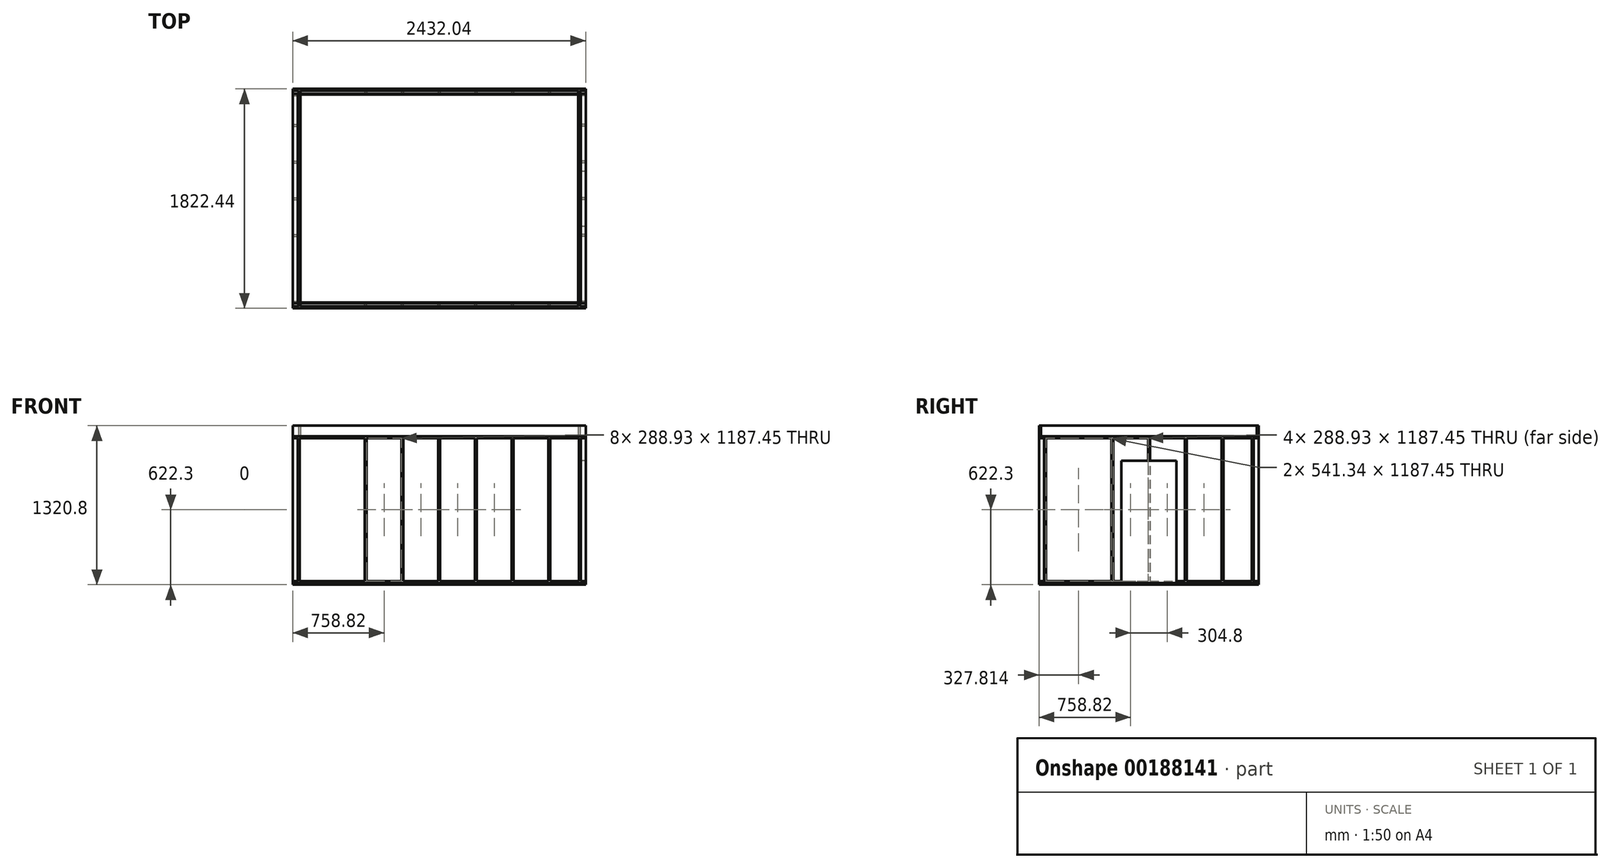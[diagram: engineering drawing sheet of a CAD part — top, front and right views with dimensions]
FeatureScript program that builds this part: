
annotation { "Feature Type Name" : "Feature", "Feature Type Description" : "" }
export const myFeature = defineFeature(function(context is Context, id is Id, definition is map)
    precondition{}
    {
        {
            var Q0;
            Q0=qCreatedBy(makeId("Top.planeOp"),FACE);
            var sketch = newSketch(context, id + "F0", { "sketchPlane" : qUnion([Q0])});
            skLineSegment(sketch, "E0.bottom", {"start": v(1174.75, 869.95) * mm, "end": v(-1174.75, 869.95) * mm});
            skLineSegment(sketch, "E0.top", {"start": v(1174.75, -869.95) * mm, "end": v(-1174.75, -869.95) * mm});
            skLineSegment(sketch, "E0.left", {"start": v(1174.75, 869.95) * mm, "end": v(1174.75, -869.95) * mm});
            skLineSegment(sketch, "E0.right", {"start": v(-1174.75, 869.95) * mm, "end": v(-1174.75, -869.95) * mm});
            skPoint(sketch, "E0.middle", {"position": v(0, 0) * mm});
            skLineSegment(sketch, "E1.0", {"start": v(1168.4, 863.6) * mm, "end": v(-1168.4, 863.6) * mm});
            skLineSegment(sketch, "E1.1", {"start": v(1168.4, 863.6) * mm, "end": v(1168.4, -863.6) * mm});
            skLineSegment(sketch, "E1.2", {"start": v(1168.4, -863.6) * mm, "end": v(-1168.4, -863.6) * mm});
            skLineSegment(sketch, "E1.3", {"start": v(-1168.4, 863.6) * mm, "end": v(-1168.4, -863.6) * mm});
            skSolve(sketch);
        }
        {
            var Q0;
            Q0 = qSketchRegion(id + "F0", true);
            extrude(context, id + "F1", {"entities" : qUnion([Q0]), "depth" : 1219.2 * mm});
        }
        {
            var Q0;
            Q0=makeQuery(id+"F1.opExtrude","SWEPT_FACE",FACE,{"disambiguationData":[OSD([sQuery(id+"F0.wireOp",EDGE,"E0.top")])]});
            var sketch = newSketch(context, id + "F2", { "sketchPlane" : qUnion([Q0])});
            skLineSegment(sketch, "E2.bottom", {"start": v(-1216.03, 0) * mm, "end": v(1216.03, 0) * mm});
            skLineSegment(sketch, "E2.top", {"start": v(-1216.03, 15.87) * mm, "end": v(1216.03, 15.87) * mm});
            skLineSegment(sketch, "E2.left", {"start": v(-1216.03, 0) * mm, "end": v(-1216.03, 15.87) * mm});
            skLineSegment(sketch, "E2.right", {"start": v(1216.03, 0) * mm, "end": v(1216.03, 15.87) * mm});
            skLineSegment(sketch, "E3.bottom", {"start": v(1216.03, 1219.2) * mm, "end": v(-1216.03, 1219.2) * mm});
            skLineSegment(sketch, "E3.top", {"start": v(1216.03, 1203.33) * mm, "end": v(-1216.03, 1203.32) * mm});
            skLineSegment(sketch, "E3.left", {"start": v(1216.03, 1219.2) * mm, "end": v(1216.03, 1203.33) * mm});
            skLineSegment(sketch, "E3.right", {"start": v(-1216.03, 1219.2) * mm, "end": v(-1216.03, 1203.32) * mm});
            skLineSegment(sketch, "E4.bottom", {"start": v(-1174.75, 1203.32) * mm, "end": v(-1158.88, 1203.32) * mm});
            skLineSegment(sketch, "E4.top", {"start": v(-1174.75, 15.87) * mm, "end": v(-1158.88, 15.87) * mm});
            skLineSegment(sketch, "E4.left", {"start": v(-1174.75, 1203.32) * mm, "end": v(-1174.75, 15.87) * mm});
            skLineSegment(sketch, "E4.right", {"start": v(-1158.88, 1203.32) * mm, "end": v(-1158.88, 15.87) * mm});
            skLineSegment(sketch, "E5.bottom", {"start": v(1174.75, 1203.33) * mm, "end": v(1158.88, 1203.33) * mm});
            skLineSegment(sketch, "E5.top", {"start": v(1174.75, 15.87) * mm, "end": v(1158.88, 15.87) * mm});
            skLineSegment(sketch, "E5.left", {"start": v(1174.75, 1203.33) * mm, "end": v(1174.75, 15.87) * mm});
            skLineSegment(sketch, "E5.right", {"start": v(1158.88, 1203.33) * mm, "end": v(1158.88, 15.88) * mm});
            skLineSegment(sketch, "E6.bottom", {"start": v(-922.34, 1203.32) * mm, "end": v(-906.46, 1203.32) * mm});
            skLineSegment(sketch, "E6.top", {"start": v(-922.34, 15.87) * mm, "end": v(-906.46, 15.87) * mm});
            skLineSegment(sketch, "E6.left", {"start": v(-922.34, 1203.33) * mm, "end": v(-922.34, 15.87) * mm});
            skLineSegment(sketch, "E6.right", {"start": v(-906.46, 1203.33) * mm, "end": v(-906.46, 15.87) * mm});
            skLineSegment(sketch, "E7.1.0.0", {"start": v(-601.66, 1203.33) * mm, "end": v(-601.66, 15.87) * mm});
            skLineSegment(sketch, "E7.1.0.1", {"start": v(-617.54, 1203.33) * mm, "end": v(-617.54, 15.87) * mm});
            skLineSegment(sketch, "E7.1.0.2", {"start": v(-617.54, 1203.32) * mm, "end": v(-601.66, 1203.32) * mm});
            skLineSegment(sketch, "E7.1.0.3", {"start": v(-617.54, 15.87) * mm, "end": v(-601.66, 15.87) * mm});
            skLineSegment(sketch, "E7.2.0.0", {"start": v(-296.86, 1203.33) * mm, "end": v(-296.86, 15.87) * mm});
            skLineSegment(sketch, "E7.2.0.1", {"start": v(-312.74, 1203.33) * mm, "end": v(-312.74, 15.87) * mm});
            skLineSegment(sketch, "E7.2.0.2", {"start": v(-312.74, 1203.32) * mm, "end": v(-296.86, 1203.32) * mm});
            skLineSegment(sketch, "E7.2.0.3", {"start": v(-312.74, 15.87) * mm, "end": v(-296.86, 15.87) * mm});
            skLineSegment(sketch, "E7.3.0.0", {"start": v(7.94, 1203.33) * mm, "end": v(7.94, 15.87) * mm});
            skLineSegment(sketch, "E7.3.0.1", {"start": v(-7.94, 1203.33) * mm, "end": v(-7.94, 15.87) * mm});
            skLineSegment(sketch, "E7.3.0.2", {"start": v(-7.94, 1203.32) * mm, "end": v(7.94, 1203.32) * mm});
            skLineSegment(sketch, "E7.3.0.3", {"start": v(-7.94, 15.87) * mm, "end": v(7.94, 15.87) * mm});
            skLineSegment(sketch, "E7.4.0.0", {"start": v(312.74, 1203.33) * mm, "end": v(312.74, 15.87) * mm});
            skLineSegment(sketch, "E7.4.0.1", {"start": v(296.86, 1203.33) * mm, "end": v(296.86, 15.87) * mm});
            skLineSegment(sketch, "E7.4.0.2", {"start": v(296.86, 1203.32) * mm, "end": v(312.74, 1203.32) * mm});
            skLineSegment(sketch, "E7.4.0.3", {"start": v(296.86, 15.87) * mm, "end": v(312.74, 15.87) * mm});
            skLineSegment(sketch, "E7.5.0.0", {"start": v(617.54, 1203.33) * mm, "end": v(617.54, 15.87) * mm});
            skLineSegment(sketch, "E7.5.0.1", {"start": v(601.66, 1203.33) * mm, "end": v(601.66, 15.87) * mm});
            skLineSegment(sketch, "E7.5.0.2", {"start": v(601.66, 1203.32) * mm, "end": v(617.54, 1203.32) * mm});
            skLineSegment(sketch, "E7.5.0.3", {"start": v(601.66, 15.87) * mm, "end": v(617.54, 15.87) * mm});
            skLineSegment(sketch, "E7.6.0.0", {"start": v(922.34, 1203.33) * mm, "end": v(922.34, 15.87) * mm});
            skLineSegment(sketch, "E7.6.0.1", {"start": v(906.46, 1203.33) * mm, "end": v(906.46, 15.87) * mm});
            skLineSegment(sketch, "E7.6.0.2", {"start": v(906.46, 1203.32) * mm, "end": v(922.34, 1203.32) * mm});
            skLineSegment(sketch, "E7.6.0.3", {"start": v(906.46, 15.87) * mm, "end": v(922.34, 15.87) * mm});
            skLineSegment(sketch, "E7.direction1", {"start": v(-906.46, 15.87) * mm, "end": v(-601.66, 15.87) * mm, "construction": true});
            skLineSegment(sketch, "E8", {"start": v(-1158.88, 609.6) * mm, "end": v(-922.34, 609.6) * mm, "construction": true});
            skLineSegment(sketch, "E9", {"start": v(922.34, 609.6) * mm, "end": v(1158.88, 609.6) * mm, "construction": true});
            skSolve(sketch);
        }
        {
            var Q0;
            Q0 = qSketchRegion(id + "F2", true);
            var Q1;
            Q1=makeQuery(id+"F2.imprint","IMPRINT",FACE,{"disambiguationData":[TD([[makeQuery(id+"F2.imprint","IMPRINT",EDGE,{"derivedFrom":sQuery(id+"F2.wireOp",EDGE,"E6.bottom")}),-1.0]])]});
            var Q2;
            Q2=makeQuery(id+"F2.imprint","IMPRINT",FACE,{"disambiguationData":[TD([[makeQuery(id+"F2.imprint","IMPRINT",EDGE,{"derivedFrom":sQuery(id+"F2.wireOp",EDGE,"E7.1.0.0")}),-1.0]])]});
            var Q3;
            Q3=makeQuery(id+"F2.imprint","IMPRINT",FACE,{"disambiguationData":[TD([[makeQuery(id+"F2.imprint","IMPRINT",EDGE,{"derivedFrom":sQuery(id+"F2.wireOp",EDGE,"E7.2.0.0")}),-1.0]])]});
            var Q4;
            Q4=makeQuery(id+"F2.imprint","IMPRINT",FACE,{"disambiguationData":[TD([[makeQuery(id+"F2.imprint","IMPRINT",EDGE,{"derivedFrom":sQuery(id+"F2.wireOp",EDGE,"E7.3.0.0")}),-1.0]])]});
            var Q5;
            Q5=makeQuery(id+"F2.imprint","IMPRINT",FACE,{"disambiguationData":[TD([[makeQuery(id+"F2.imprint","IMPRINT",EDGE,{"derivedFrom":sQuery(id+"F2.wireOp",EDGE,"E7.4.0.0")}),-1.0]])]});
            var Q6;
            Q6=makeQuery(id+"F2.imprint","IMPRINT",FACE,{"disambiguationData":[TD([[makeQuery(id+"F2.imprint","IMPRINT",EDGE,{"derivedFrom":sQuery(id+"F2.wireOp",EDGE,"E7.5.0.0")}),-1.0]])]});
            var Q7;
            Q7=makeQuery(id+"F2.imprint","IMPRINT",FACE,{"disambiguationData":[TD([[makeQuery(id+"F2.imprint","IMPRINT",EDGE,{"derivedFrom":sQuery(id+"F2.wireOp",EDGE,"E7.6.0.0")}),-1.0]])]});
            extrude(context, id + "F3", {"entities" : qUnion([Q0, Q1, Q2, Q3, Q4, Q5, Q6, Q7]), "depth" : 41.27 * mm});
        }
        {
            var Q0;
            Q0=makeQuery(id+"F3.opExtrude","SWEPT_BODY",BODY,{"disambiguationData":[OSD([sQuery(id+"F2.wireOp",EDGE,"E2.bottom"),sQuery(id+"F2.wireOp",EDGE,"E2.top"),sQuery(id+"F2.wireOp",EDGE,"E2.left"),sQuery(id+"F2.wireOp",EDGE,"E2.right"),sQuery(id+"F2.wireOp",EDGE,"E3.bottom"),sQuery(id+"F2.wireOp",EDGE,"E3.top"),sQuery(id+"F2.wireOp",EDGE,"E3.left"),sQuery(id+"F2.wireOp",EDGE,"E3.right"),sQuery(id+"F2.wireOp",EDGE,"E4.left"),sQuery(id+"F2.wireOp",EDGE,"E4.right"),sQuery(id+"F2.wireOp",EDGE,"E5.left"),sQuery(id+"F2.wireOp",EDGE,"E5.right"),sQuery(id+"F2.wireOp",EDGE,"E6.left"),sQuery(id+"F2.wireOp",EDGE,"E6.right"),sQuery(id+"F2.wireOp",EDGE,"E7.1.0.0"),sQuery(id+"F2.wireOp",EDGE,"E7.1.0.1"),sQuery(id+"F2.wireOp",EDGE,"E7.2.0.0"),sQuery(id+"F2.wireOp",EDGE,"E7.2.0.1"),sQuery(id+"F2.wireOp",EDGE,"E7.3.0.0"),sQuery(id+"F2.wireOp",EDGE,"E7.3.0.1"),sQuery(id+"F2.wireOp",EDGE,"E7.4.0.0"),sQuery(id+"F2.wireOp",EDGE,"E7.4.0.1"),sQuery(id+"F2.wireOp",EDGE,"E7.5.0.0"),sQuery(id+"F2.wireOp",EDGE,"E7.5.0.1"),sQuery(id+"F2.wireOp",EDGE,"E7.6.0.0"),sQuery(id+"F2.wireOp",EDGE,"E7.6.0.1")])]});
            var Q1;
            Q1=qCreatedBy(makeId("Front.planeOp"),FACE);
            mirror(context, id + "F4", {"entities" : qUnion([Q0]), "mirrorPlane" : qUnion([Q1])});
        }
        {
            var Q0;
            Q0=makeQuery(id+"F1.opExtrude","SWEPT_FACE",FACE,{"disambiguationData":[OSD([sQuery(id+"F0.wireOp",EDGE,"E0.left")])]});
            var sketch = newSketch(context, id + "F5", { "sketchPlane" : qUnion([Q0])});
            skLineSegment(sketch, "E10.bottom", {"start": v(-869.95, 0) * mm, "end": v(869.95, 0) * mm});
            skLineSegment(sketch, "E10.top", {"start": v(-869.95, 15.87) * mm, "end": v(869.95, 15.87) * mm});
            skLineSegment(sketch, "E10.left", {"start": v(-869.95, 0) * mm, "end": v(-869.95, 15.87) * mm});
            skLineSegment(sketch, "E10.right", {"start": v(869.95, 0) * mm, "end": v(869.95, 15.87) * mm});
            skLineSegment(sketch, "E11.bottom", {"start": v(-869.95, 1219.2) * mm, "end": v(869.95, 1219.2) * mm});
            skLineSegment(sketch, "E11.top", {"start": v(-869.95, 1203.33) * mm, "end": v(869.95, 1203.33) * mm});
            skLineSegment(sketch, "E11.left", {"start": v(-869.95, 1219.2) * mm, "end": v(-869.95, 1203.33) * mm});
            skLineSegment(sketch, "E11.right", {"start": v(869.95, 1219.2) * mm, "end": v(869.95, 1203.33) * mm});
            skLineSegment(sketch, "E12.bottom", {"start": v(-869.95, 1203.33) * mm, "end": v(-854.08, 1203.33) * mm});
            skLineSegment(sketch, "E12.top", {"start": v(-869.95, 15.87) * mm, "end": v(-854.08, 15.87) * mm});
            skLineSegment(sketch, "E12.left", {"start": v(-869.95, 1203.33) * mm, "end": v(-869.95, 15.87) * mm});
            skLineSegment(sketch, "E12.right", {"start": v(-854.08, 1203.33) * mm, "end": v(-854.08, 15.87) * mm});
            skLineSegment(sketch, "E13.bottom", {"start": v(869.95, 1203.33) * mm, "end": v(854.08, 1203.33) * mm});
            skLineSegment(sketch, "E13.top", {"start": v(869.95, 15.87) * mm, "end": v(854.08, 15.87) * mm});
            skLineSegment(sketch, "E13.left", {"start": v(869.95, 1203.33) * mm, "end": v(869.95, 15.87) * mm});
            skLineSegment(sketch, "E13.right", {"start": v(854.08, 1203.33) * mm, "end": v(854.08, 15.87) * mm});
            skLineSegment(sketch, "E14.bottom", {"start": v(-617.54, 1203.33) * mm, "end": v(-601.66, 1203.33) * mm});
            skLineSegment(sketch, "E14.top", {"start": v(-617.54, 15.87) * mm, "end": v(-601.66, 15.87) * mm});
            skLineSegment(sketch, "E14.left", {"start": v(-617.54, 1203.33) * mm, "end": v(-617.54, 15.87) * mm});
            skLineSegment(sketch, "E14.right", {"start": v(-601.66, 1203.33) * mm, "end": v(-601.66, 15.87) * mm});
            skLineSegment(sketch, "E15.1.0.0", {"start": v(-296.86, 1203.33) * mm, "end": v(-296.86, 15.87) * mm});
            skLineSegment(sketch, "E15.1.0.1", {"start": v(-312.74, 1203.33) * mm, "end": v(-312.74, 15.87) * mm});
            skLineSegment(sketch, "E15.1.0.2", {"start": v(-312.74, 1203.33) * mm, "end": v(-296.86, 1203.33) * mm});
            skLineSegment(sketch, "E15.1.0.3", {"start": v(-312.74, 15.87) * mm, "end": v(-296.86, 15.87) * mm});
            skLineSegment(sketch, "E15.2.0.0", {"start": v(7.94, 1203.33) * mm, "end": v(7.94, 15.87) * mm});
            skLineSegment(sketch, "E15.2.0.1", {"start": v(-7.94, 1203.33) * mm, "end": v(-7.94, 15.87) * mm});
            skLineSegment(sketch, "E15.2.0.2", {"start": v(-7.94, 1203.33) * mm, "end": v(7.94, 1203.33) * mm});
            skLineSegment(sketch, "E15.2.0.3", {"start": v(-7.94, 15.87) * mm, "end": v(7.94, 15.87) * mm});
            skLineSegment(sketch, "E15.3.0.0", {"start": v(312.74, 1203.33) * mm, "end": v(312.74, 15.87) * mm});
            skLineSegment(sketch, "E15.3.0.1", {"start": v(296.86, 1203.33) * mm, "end": v(296.86, 15.87) * mm});
            skLineSegment(sketch, "E15.3.0.2", {"start": v(296.86, 1203.33) * mm, "end": v(312.74, 1203.33) * mm});
            skLineSegment(sketch, "E15.3.0.3", {"start": v(296.86, 15.87) * mm, "end": v(312.74, 15.87) * mm});
            skLineSegment(sketch, "E15.4.0.0", {"start": v(617.54, 1203.33) * mm, "end": v(617.54, 15.87) * mm});
            skLineSegment(sketch, "E15.4.0.1", {"start": v(601.66, 1203.33) * mm, "end": v(601.66, 15.87) * mm});
            skLineSegment(sketch, "E15.4.0.2", {"start": v(601.66, 1203.33) * mm, "end": v(617.54, 1203.33) * mm});
            skLineSegment(sketch, "E15.4.0.3", {"start": v(601.66, 15.87) * mm, "end": v(617.54, 15.87) * mm});
            skLineSegment(sketch, "E15.direction1", {"start": v(-601.66, 15.87) * mm, "end": v(-296.86, 15.87) * mm, "construction": true});
            skLineSegment(sketch, "E16", {"start": v(-854.08, 609.6) * mm, "end": v(-617.54, 609.6) * mm, "construction": true});
            skLineSegment(sketch, "E17", {"start": v(617.54, 609.6) * mm, "end": v(854.08, 609.6) * mm, "construction": true});
            skSolve(sketch);
        }
        {
            var Q0;
            Q0 = qSketchRegion(id + "F5", true);
            var Q1;
            Q1=makeQuery(id+"F5.imprint","IMPRINT",FACE,{"disambiguationData":[TD([[makeQuery(id+"F5.imprint","IMPRINT",EDGE,{"derivedFrom":sQuery(id+"F5.wireOp",EDGE,"E14.bottom")}),-1.0]])]});
            var Q2;
            Q2=makeQuery(id+"F5.imprint","IMPRINT",FACE,{"disambiguationData":[TD([[makeQuery(id+"F5.imprint","IMPRINT",EDGE,{"derivedFrom":sQuery(id+"F5.wireOp",EDGE,"E15.1.0.0")}),-1.0]])]});
            var Q3;
            Q3=makeQuery(id+"F5.imprint","IMPRINT",FACE,{"disambiguationData":[TD([[makeQuery(id+"F5.imprint","IMPRINT",EDGE,{"derivedFrom":sQuery(id+"F5.wireOp",EDGE,"E15.2.0.0")}),-1.0]])]});
            var Q4;
            Q4=makeQuery(id+"F5.imprint","IMPRINT",FACE,{"disambiguationData":[TD([[makeQuery(id+"F5.imprint","IMPRINT",EDGE,{"derivedFrom":sQuery(id+"F5.wireOp",EDGE,"E15.3.0.0")}),-1.0]])]});
            var Q5;
            Q5=makeQuery(id+"F5.imprint","IMPRINT",FACE,{"disambiguationData":[TD([[makeQuery(id+"F5.imprint","IMPRINT",EDGE,{"derivedFrom":sQuery(id+"F5.wireOp",EDGE,"E15.4.0.0")}),-1.0]])]});
            extrude(context, id + "F6", {"entities" : qUnion([Q0, Q1, Q2, Q3, Q4, Q5]), "depth" : 41.27 * mm});
        }
        {
            var Q0;
            Q0=makeQuery(id+"F6.opExtrude","SWEPT_BODY",BODY,{"disambiguationData":[OSD([sQuery(id+"F5.wireOp",EDGE,"E10.bottom"),sQuery(id+"F5.wireOp",EDGE,"E10.top"),sQuery(id+"F5.wireOp",EDGE,"E10.left"),sQuery(id+"F5.wireOp",EDGE,"E10.right"),sQuery(id+"F5.wireOp",EDGE,"E11.bottom"),sQuery(id+"F5.wireOp",EDGE,"E11.top"),sQuery(id+"F5.wireOp",EDGE,"E11.left"),sQuery(id+"F5.wireOp",EDGE,"E11.right"),sQuery(id+"F5.wireOp",EDGE,"E12.left"),sQuery(id+"F5.wireOp",EDGE,"E12.right"),sQuery(id+"F5.wireOp",EDGE,"E13.left"),sQuery(id+"F5.wireOp",EDGE,"E13.right"),sQuery(id+"F5.wireOp",EDGE,"E14.left"),sQuery(id+"F5.wireOp",EDGE,"E14.right"),sQuery(id+"F5.wireOp",EDGE,"E15.1.0.0"),sQuery(id+"F5.wireOp",EDGE,"E15.1.0.1"),sQuery(id+"F5.wireOp",EDGE,"E15.2.0.0"),sQuery(id+"F5.wireOp",EDGE,"E15.2.0.1"),sQuery(id+"F5.wireOp",EDGE,"E15.3.0.0"),sQuery(id+"F5.wireOp",EDGE,"E15.3.0.1"),sQuery(id+"F5.wireOp",EDGE,"E15.4.0.0"),sQuery(id+"F5.wireOp",EDGE,"E15.4.0.1")])]});
            var Q1;
            Q1=qCreatedBy(makeId("Right.planeOp"),FACE);
            mirror(context, id + "F7", {"entities" : qUnion([Q0]), "mirrorPlane" : qUnion([Q1])});
        }
        {
            var Q0;
            Q0=makeQuery(id+"F3.opExtrude","SWEPT_FACE",FACE,{"disambiguationData":[OSD([sQuery(id+"F2.wireOp",EDGE,"E3.bottom")])]});
            var sketch = newSketch(context, id + "F8", { "sketchPlane" : qUnion([Q0])});
            skLineSegment(sketch, "E18.bottom", {"start": v(-1168.4, 863.6) * mm, "end": v(1168.4, 863.6) * mm});
            skLineSegment(sketch, "E18.top", {"start": v(-1168.4, -863.6) * mm, "end": v(1168.4, -863.6) * mm});
            skLineSegment(sketch, "E18.left", {"start": v(-1168.4, 863.6) * mm, "end": v(-1168.4, -863.6) * mm});
            skLineSegment(sketch, "E18.right", {"start": v(1168.4, 863.6) * mm, "end": v(1168.4, -863.6) * mm});
            skSolve(sketch);
        }
        {
            var Q0;
            Q0=makeQuery(id+"F8.imprint","IMPRINT",FACE,{"disambiguationData":[TD([[makeQuery(id+"F8.imprint","IMPRINT",EDGE,{"derivedFrom":sQuery(id+"F8.wireOp",EDGE,"E18.bottom")}),-1.0]])]});
            extrude(context, id + "F9", {"entities" : qUnion([Q0]), "oppositeDirection" : true, "depth" : 6.35 * mm});
        }
        {
            var Q0;
            Q0=makeQuery(id+"F3.opExtrude","SWEPT_FACE",FACE,{"disambiguationData":[OSD([sQuery(id+"F2.wireOp",EDGE,"E3.bottom")])]});
            var sketch = newSketch(context, id + "F10", { "sketchPlane" : qUnion([Q0])});
            skLineSegment(sketch, "E19.bottom", {"start": v(-1216.03, 911.23) * mm, "end": v(1216.03, 911.23) * mm});
            skLineSegment(sketch, "E19.top", {"start": v(-1216.03, 895.35) * mm, "end": v(1216.03, 895.35) * mm});
            skLineSegment(sketch, "E19.left", {"start": v(-1216.03, 911.23) * mm, "end": v(-1216.03, 895.35) * mm});
            skLineSegment(sketch, "E19.right", {"start": v(1216.03, 911.23) * mm, "end": v(1216.03, 895.35) * mm});
            skLineSegment(sketch, "E20.bottom", {"start": v(1216.03, -911.23) * mm, "end": v(-1216.03, -911.23) * mm});
            skLineSegment(sketch, "E20.top", {"start": v(1216.03, -895.35) * mm, "end": v(-1216.03, -895.35) * mm});
            skLineSegment(sketch, "E20.left", {"start": v(1216.03, -911.23) * mm, "end": v(1216.03, -895.35) * mm});
            skLineSegment(sketch, "E20.right", {"start": v(-1216.03, -911.23) * mm, "end": v(-1216.03, -895.35) * mm});
            skLineSegment(sketch, "E21.bottom", {"start": v(-1168.4, 895.35) * mm, "end": v(-1152.53, 895.35) * mm});
            skLineSegment(sketch, "E21.top", {"start": v(-1168.4, -895.35) * mm, "end": v(-1152.53, -895.35) * mm});
            skLineSegment(sketch, "E21.left", {"start": v(-1168.4, 895.35) * mm, "end": v(-1168.4, -895.35) * mm});
            skLineSegment(sketch, "E21.right", {"start": v(-1152.53, 895.35) * mm, "end": v(-1152.53, -895.35) * mm});
            skLineSegment(sketch, "E22.bottom", {"start": v(1168.4, 895.35) * mm, "end": v(1152.52, 895.35) * mm});
            skLineSegment(sketch, "E22.top", {"start": v(1168.4, -895.35) * mm, "end": v(1152.53, -895.35) * mm});
            skLineSegment(sketch, "E22.left", {"start": v(1168.4, 895.35) * mm, "end": v(1168.4, -895.35) * mm});
            skLineSegment(sketch, "E22.right", {"start": v(1152.52, 895.35) * mm, "end": v(1152.53, -895.35) * mm});
            skLineSegment(sketch, "E23.bottom", {"start": v(-922.34, 895.35) * mm, "end": v(-906.46, 895.35) * mm});
            skLineSegment(sketch, "E23.top", {"start": v(-922.34, -895.35) * mm, "end": v(-906.46, -895.35) * mm});
            skLineSegment(sketch, "E23.left", {"start": v(-922.34, 895.35) * mm, "end": v(-922.34, -895.35) * mm});
            skLineSegment(sketch, "E23.right", {"start": v(-906.46, 895.35) * mm, "end": v(-906.46, -895.35) * mm});
            skLineSegment(sketch, "E24.1.0.0", {"start": v(-601.66, 895.35) * mm, "end": v(-601.66, -895.35) * mm});
            skLineSegment(sketch, "E24.1.0.1", {"start": v(-617.54, 895.35) * mm, "end": v(-617.54, -895.35) * mm});
            skLineSegment(sketch, "E24.1.0.2", {"start": v(-617.54, 895.35) * mm, "end": v(-601.66, 895.35) * mm});
            skLineSegment(sketch, "E24.1.0.3", {"start": v(-617.54, -895.35) * mm, "end": v(-601.66, -895.35) * mm});
            skLineSegment(sketch, "E24.2.0.0", {"start": v(-296.86, 895.35) * mm, "end": v(-296.86, -895.35) * mm});
            skLineSegment(sketch, "E24.2.0.1", {"start": v(-312.74, 895.35) * mm, "end": v(-312.74, -895.35) * mm});
            skLineSegment(sketch, "E24.2.0.2", {"start": v(-312.74, 895.35) * mm, "end": v(-296.86, 895.35) * mm});
            skLineSegment(sketch, "E24.2.0.3", {"start": v(-312.74, -895.35) * mm, "end": v(-296.86, -895.35) * mm});
            skLineSegment(sketch, "E24.3.0.0", {"start": v(7.94, 895.35) * mm, "end": v(7.94, -895.35) * mm});
            skLineSegment(sketch, "E24.3.0.1", {"start": v(-7.94, 895.35) * mm, "end": v(-7.94, -895.35) * mm});
            skLineSegment(sketch, "E24.3.0.2", {"start": v(-7.94, 895.35) * mm, "end": v(7.94, 895.35) * mm});
            skLineSegment(sketch, "E24.3.0.3", {"start": v(-7.94, -895.35) * mm, "end": v(7.94, -895.35) * mm});
            skLineSegment(sketch, "E24.4.0.0", {"start": v(312.74, 895.35) * mm, "end": v(312.74, -895.35) * mm});
            skLineSegment(sketch, "E24.4.0.1", {"start": v(296.86, 895.35) * mm, "end": v(296.86, -895.35) * mm});
            skLineSegment(sketch, "E24.4.0.2", {"start": v(296.86, 895.35) * mm, "end": v(312.74, 895.35) * mm});
            skLineSegment(sketch, "E24.4.0.3", {"start": v(296.86, -895.35) * mm, "end": v(312.74, -895.35) * mm});
            skLineSegment(sketch, "E24.5.0.0", {"start": v(617.54, 895.35) * mm, "end": v(617.54, -895.35) * mm});
            skLineSegment(sketch, "E24.5.0.1", {"start": v(601.66, 895.35) * mm, "end": v(601.66, -895.35) * mm});
            skLineSegment(sketch, "E24.5.0.2", {"start": v(601.66, 895.35) * mm, "end": v(617.54, 895.35) * mm});
            skLineSegment(sketch, "E24.5.0.3", {"start": v(601.66, -895.35) * mm, "end": v(617.54, -895.35) * mm});
            skLineSegment(sketch, "E24.6.0.0", {"start": v(922.34, 895.35) * mm, "end": v(922.34, -895.35) * mm});
            skLineSegment(sketch, "E24.6.0.1", {"start": v(906.46, 895.35) * mm, "end": v(906.46, -895.35) * mm});
            skLineSegment(sketch, "E24.6.0.2", {"start": v(906.46, 895.35) * mm, "end": v(922.34, 895.35) * mm});
            skLineSegment(sketch, "E24.6.0.3", {"start": v(906.46, -895.35) * mm, "end": v(922.34, -895.35) * mm});
            skLineSegment(sketch, "E24.direction1", {"start": v(-906.46, -895.35) * mm, "end": v(-601.66, -895.35) * mm, "construction": true});
            skLineSegment(sketch, "E25", {"start": v(-1152.53, 0) * mm, "end": v(-922.34, 0) * mm, "construction": true});
            skLineSegment(sketch, "E26", {"start": v(922.34, 0) * mm, "end": v(1152.53, 0) * mm, "construction": true});
            skSolve(sketch);
        }
        {
            var Q0;
            Q0 = qSketchRegion(id + "F10", true);
            var Q1;
            {var subQ0=sQuery(id+"F10.wireOp",EDGE,"E23.bottom");Q1=makeQuery(id+"F10.imprint","IMPRINT",FACE,{"disambiguationData":[TD([[makeQuery(id+"F10.imprint","IMPRINT",EDGE,{"derivedFrom":subQ0}),-1.0]])]});}
            var Q2;
            {var subQ0=sQuery(id+"F10.wireOp",EDGE,"E24.1.0.2");Q2=makeQuery(id+"F10.imprint","IMPRINT",FACE,{"disambiguationData":[TD([[makeQuery(id+"F10.imprint","IMPRINT",EDGE,{"derivedFrom":subQ0}),-1.0]])]});}
            var Q3;
            {var subQ0=sQuery(id+"F10.wireOp",EDGE,"E24.2.0.2");Q3=makeQuery(id+"F10.imprint","IMPRINT",FACE,{"disambiguationData":[TD([[makeQuery(id+"F10.imprint","IMPRINT",EDGE,{"derivedFrom":subQ0}),-1.0]])]});}
            var Q4;
            {var subQ0=sQuery(id+"F10.wireOp",EDGE,"E24.3.0.2");Q4=makeQuery(id+"F10.imprint","IMPRINT",FACE,{"disambiguationData":[TD([[makeQuery(id+"F10.imprint","IMPRINT",EDGE,{"derivedFrom":subQ0}),-1.0]])]});}
            var Q5;
            {var subQ0=sQuery(id+"F10.wireOp",EDGE,"E24.4.0.2");Q5=makeQuery(id+"F10.imprint","IMPRINT",FACE,{"disambiguationData":[TD([[makeQuery(id+"F10.imprint","IMPRINT",EDGE,{"derivedFrom":subQ0}),-1.0]])]});}
            var Q6;
            {var subQ0=sQuery(id+"F10.wireOp",EDGE,"E24.5.0.2");Q6=makeQuery(id+"F10.imprint","IMPRINT",FACE,{"disambiguationData":[TD([[makeQuery(id+"F10.imprint","IMPRINT",EDGE,{"derivedFrom":subQ0}),-1.0]])]});}
            var Q7;
            {var subQ0=sQuery(id+"F10.wireOp",EDGE,"E24.6.0.2");Q7=makeQuery(id+"F10.imprint","IMPRINT",FACE,{"disambiguationData":[TD([[makeQuery(id+"F10.imprint","IMPRINT",EDGE,{"derivedFrom":subQ0}),-1.0]])]});}
            var Q8;
            {var subQ0=sQuery(id+"F10.wireOp",EDGE,"E24.6.0.3");Q8=makeQuery(id+"F10.imprint","IMPRINT",FACE,{"disambiguationData":[TD([[makeQuery(id+"F10.imprint","IMPRINT",EDGE,{"derivedFrom":subQ0}),1.0]])]});}
            var Q9;
            {var subQ0=sQuery(id+"F10.wireOp",EDGE,"E24.5.0.3");Q9=makeQuery(id+"F10.imprint","IMPRINT",FACE,{"disambiguationData":[TD([[makeQuery(id+"F10.imprint","IMPRINT",EDGE,{"derivedFrom":subQ0}),1.0]])]});}
            var Q10;
            {var subQ0=sQuery(id+"F10.wireOp",EDGE,"E24.4.0.3");Q10=makeQuery(id+"F10.imprint","IMPRINT",FACE,{"disambiguationData":[TD([[makeQuery(id+"F10.imprint","IMPRINT",EDGE,{"derivedFrom":subQ0}),1.0]])]});}
            var Q11;
            {var subQ0=sQuery(id+"F10.wireOp",EDGE,"E24.3.0.3");Q11=makeQuery(id+"F10.imprint","IMPRINT",FACE,{"disambiguationData":[TD([[makeQuery(id+"F10.imprint","IMPRINT",EDGE,{"derivedFrom":subQ0}),1.0]])]});}
            var Q12;
            {var subQ0=sQuery(id+"F10.wireOp",EDGE,"E24.2.0.3");Q12=makeQuery(id+"F10.imprint","IMPRINT",FACE,{"disambiguationData":[TD([[makeQuery(id+"F10.imprint","IMPRINT",EDGE,{"derivedFrom":subQ0}),1.0]])]});}
            var Q13;
            {var subQ0=sQuery(id+"F10.wireOp",EDGE,"E24.1.0.3");Q13=makeQuery(id+"F10.imprint","IMPRINT",FACE,{"disambiguationData":[TD([[makeQuery(id+"F10.imprint","IMPRINT",EDGE,{"derivedFrom":subQ0}),1.0]])]});}
            var Q14;
            {var subQ0=sQuery(id+"F10.wireOp",EDGE,"E23.top");Q14=makeQuery(id+"F10.imprint","IMPRINT",FACE,{"disambiguationData":[TD([[makeQuery(id+"F10.imprint","IMPRINT",EDGE,{"derivedFrom":subQ0}),1.0]])]});}
            extrude(context, id + "F11", {"entities" : qUnion([Q0, Q1, Q2, Q3, Q4, Q5, Q6, Q7, Q8, Q9, Q10, Q11, Q12, Q13, Q14]), "depth" : 88.9 * mm});
        }
        {
            var Q0;
            Q0=makeQuery(id+"F3.opExtrude","SWEPT_FACE",FACE,{"disambiguationData":[OSD([sQuery(id+"F2.wireOp",EDGE,"E2.bottom")])]});
            var sketch = newSketch(context, id + "F12", { "sketchPlane" : qUnion([Q0])});
            skLineSegment(sketch, "E27.bottom", {"start": v(-1216.03, 911.23) * mm, "end": v(1216.03, 911.23) * mm});
            skLineSegment(sketch, "E27.top", {"start": v(-1216.03, -911.23) * mm, "end": v(1216.03, -911.23) * mm});
            skLineSegment(sketch, "E27.left", {"start": v(-1216.03, 911.23) * mm, "end": v(-1216.03, -911.23) * mm});
            skLineSegment(sketch, "E27.right", {"start": v(1216.03, 911.23) * mm, "end": v(1216.03, -911.23) * mm});
            skSolve(sketch);
        }
        {
            var Q0;
            Q0 = qSketchRegion(id + "F12", true);
            extrude(context, id + "F13", {"entities" : qUnion([Q0]), "depth" : 12.7 * mm});
        }
        {
            var Q0;
            Q0=makeQuery(id+"F6.opExtrude","CAP_FACE",FACE,{"disambiguationData":[OSD([sQuery(id+"F5.wireOp",EDGE,"E10.bottom"),sQuery(id+"F5.wireOp",EDGE,"E10.top"),sQuery(id+"F5.wireOp",EDGE,"E10.left"),sQuery(id+"F5.wireOp",EDGE,"E10.right"),sQuery(id+"F5.wireOp",EDGE,"E11.bottom"),sQuery(id+"F5.wireOp",EDGE,"E11.top"),sQuery(id+"F5.wireOp",EDGE,"E11.left"),sQuery(id+"F5.wireOp",EDGE,"E11.right"),sQuery(id+"F5.wireOp",EDGE,"E12.left"),sQuery(id+"F5.wireOp",EDGE,"E12.right"),sQuery(id+"F5.wireOp",EDGE,"E13.left"),sQuery(id+"F5.wireOp",EDGE,"E13.right"),sQuery(id+"F5.wireOp",EDGE,"E14.left"),sQuery(id+"F5.wireOp",EDGE,"E14.right"),sQuery(id+"F5.wireOp",EDGE,"E15.1.0.0"),sQuery(id+"F5.wireOp",EDGE,"E15.1.0.1"),sQuery(id+"F5.wireOp",EDGE,"E15.2.0.0"),sQuery(id+"F5.wireOp",EDGE,"E15.2.0.1"),sQuery(id+"F5.wireOp",EDGE,"E15.3.0.0"),sQuery(id+"F5.wireOp",EDGE,"E15.3.0.1"),sQuery(id+"F5.wireOp",EDGE,"E15.4.0.0"),sQuery(id+"F5.wireOp",EDGE,"E15.4.0.1")])],"isStart":false});
            var sketch = newSketch(context, id + "F14", { "sketchPlane" : qUnion([Q0])});
            skLineSegment(sketch, "E28.bottom", {"start": v(-228.6, 1016) * mm, "end": v(228.6, 1016) * mm});
            skLineSegment(sketch, "E28.top", {"start": v(-228.6, 0) * mm, "end": v(228.6, 0) * mm});
            skLineSegment(sketch, "E28.left", {"start": v(-228.6, 1016) * mm, "end": v(-228.6, 0) * mm});
            skLineSegment(sketch, "E28.right", {"start": v(228.6, 1016) * mm, "end": v(228.6, 0) * mm});
            skLineSegment(sketch, "E29", {"start": v(-296.86, 609.6) * mm, "end": v(-228.6, 609.6) * mm, "construction": true});
            skLineSegment(sketch, "E30", {"start": v(296.86, 609.6) * mm, "end": v(228.6, 609.6) * mm, "construction": true});
            skSolve(sketch);
        }
        {
            var Q0;
            Q0 = qSketchRegion(id + "F14", true);
            extrude(context, id + "F15", {"entities" : qUnion([Q0]), "operationType" : NewBodyOperationType.REMOVE, "oppositeDirection" : true, "depth" : 76.2 * mm});
        }
    });
